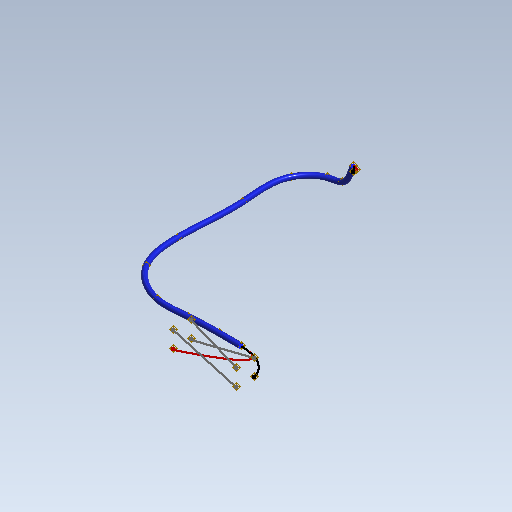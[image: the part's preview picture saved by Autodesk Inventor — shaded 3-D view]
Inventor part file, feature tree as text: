
AUTODESK INVENTOR PART (.ipt)
format: ipt  version: 2020 (Build 240168000, 168)  size: 164,864 bytes
history: native  units: mm (DEFAULTED — no unit token found)
features: other x36, plane x1, sketch x1
bodies: Body1 (feature_tree)
feature tree (38):
  other  "Origen"
  other  "Punto de trabajo5"
  other  "Punto de trabajo6"
  other  "Segmento1"
  other  "Punto de trabajo7"
  other  "Punto de trabajo8"
  other  "Punto de trabajo9"
  other  "Punto de trabajo10"
  other  "Punto de trabajo11"
  other  "Punto de trabajo12"
  other  "Punto de trabajo13"
  other  "Punto de trabajo14"
  other  "Punto de trabajo15"
  plane  "Plano de trabajo1"
  other  "Punto de trabajo16"
  other  "Punto de trabajo17"
  other  "Cable1:1"
  other  "Punto de trabajo18"
  other  "Punto de trabajo19"
  other  "Cable1:2"
  other  "Punto de trabajo20"
  other  "Punto de trabajo21"
  other  "Conductor1"
  other  "Punto de trabajo22"
  other  "Punto de trabajo23"
  other  "Conductor2"
  other  "Punto de trabajo24"
  other  "Punto de trabajo25"
  other  "Conductor3"
  other  "Plano YZ"
  other  "Plano XZ"
  other  "Plano XY"
  other  "Eje X"
  other  "Eje Y"
  other  "Eje Z"
  sketch  "Boceto1"  dims[d0=0.0mm d1=0.0mm]
  other  "Sup1"
  other  "SuperficieBarrido1"
